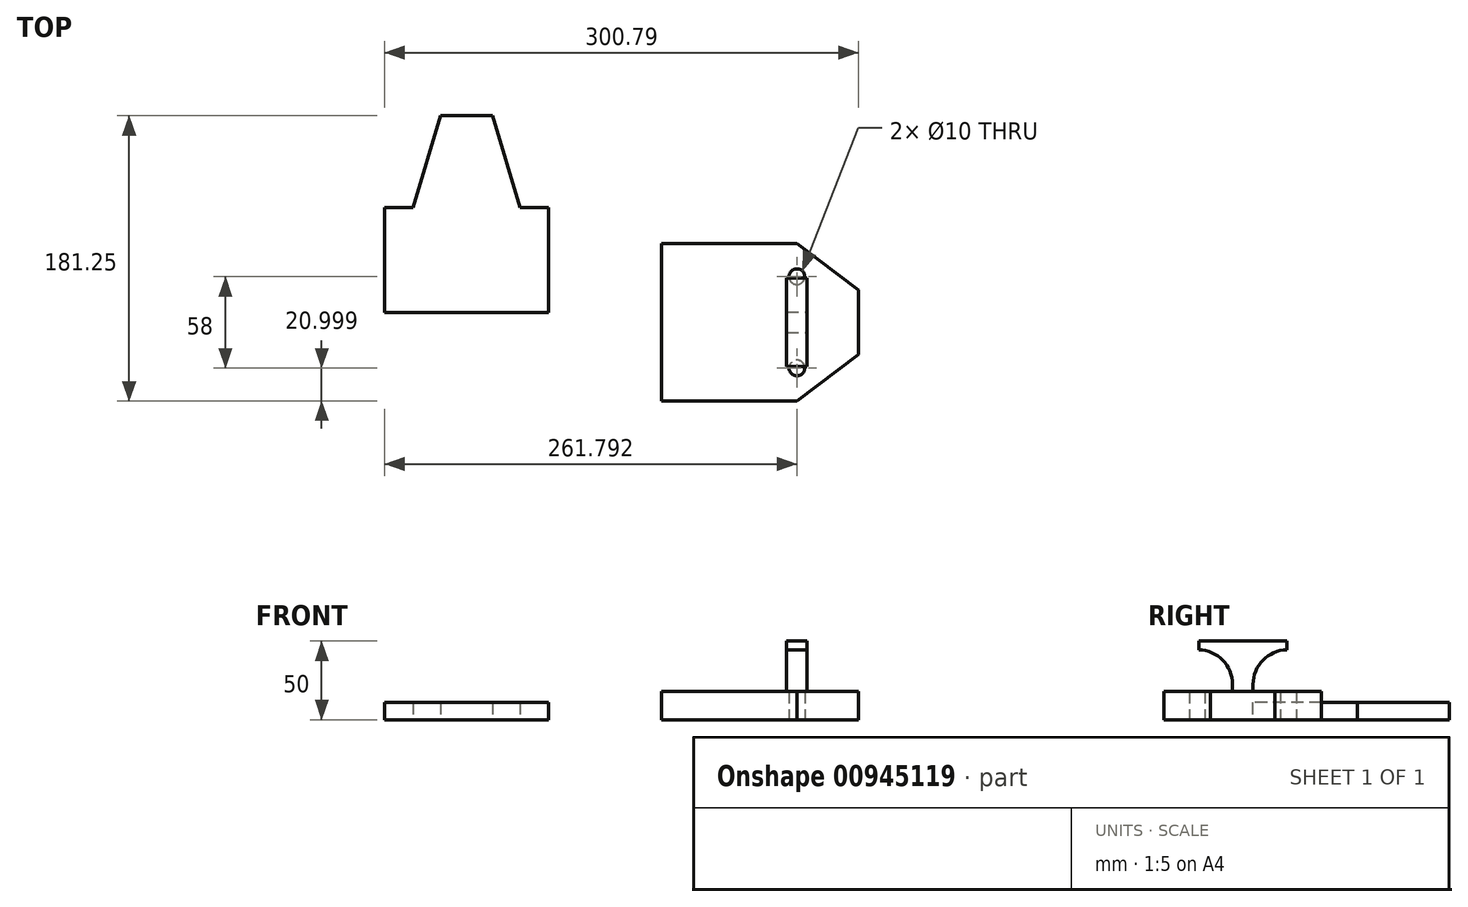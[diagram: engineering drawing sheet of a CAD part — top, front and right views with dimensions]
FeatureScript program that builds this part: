
annotation { "Feature Type Name" : "Feature", "Feature Type Description" : "" }
export const myFeature = defineFeature(function(context is Context, id is Id, definition is map)
    precondition{}
    {
        {
            var Q0;
            Q0=qCreatedBy(makeId("Top.planeOp"),FACE);
            var sketch = newSketch(context, id + "F0", { "sketchPlane" : qUnion([Q0])});
            skLineSegment(sketch, "E0.bottom", {"start": v(-75.9, 31.73) * mm, "end": v(28.1, 31.73) * mm});
            skLineSegment(sketch, "E0.top", {"start": v(-75.9, -34.77) * mm, "end": v(28.1, -34.77) * mm});
            skLineSegment(sketch, "E0.left", {"start": v(-75.9, 31.73) * mm, "end": v(-75.9, -34.77) * mm});
            skLineSegment(sketch, "E0.right", {"start": v(28.1, 31.73) * mm, "end": v(28.1, -34.77) * mm});
            skLineSegment(sketch, "E1", {"start": v(-23.9, -34.77) * mm, "end": v(-23.9, 90.23) * mm});
            skLineSegment(sketch, "E2", {"start": v(-23.9, 90.23) * mm, "end": v(-40.4, 90.23) * mm});
            skLineSegment(sketch, "E3", {"start": v(-23.9, 90.23) * mm, "end": v(-7.4, 90.23) * mm});
            skLineSegment(sketch, "E4", {"start": v(-23.9, 31.73) * mm, "end": v(-57.9, 31.73) * mm});
            skLineSegment(sketch, "E5", {"start": v(-23.9, 31.73) * mm, "end": v(10.1, 31.73) * mm});
            skLineSegment(sketch, "E6", {"start": v(10.1, 31.73) * mm, "end": v(-7.4, 90.23) * mm});
            skLineSegment(sketch, "E7.MirrorCS", {"start": v(-57.9, 31.73) * mm, "end": v(-40.4, 90.23) * mm});
            skSolve(sketch);
        }
        {
            var Q0;
            {var subQ0=sQuery(id+"F0.wireOp",EDGE,"E2");Q0=makeQuery(id+"F0.imprint","IMPRINT",FACE,{"disambiguationData":[TD([[makeQuery(id+"F0.imprint","IMPRINT",EDGE,{"derivedFrom":subQ0}),1.0]])]});}
            var Q1;
            {var subQ0=sQuery(id+"F0.wireOp",EDGE,"E3");Q1=makeQuery(id+"F0.imprint","IMPRINT",FACE,{"disambiguationData":[TD([[makeQuery(id+"F0.imprint","IMPRINT",EDGE,{"derivedFrom":subQ0}),-1.0]])]});}
            var Q2;
            {var subQ0=sQuery(id+"F0.wireOp",EDGE,"E0.right");Q2=makeQuery(id+"F0.imprint","IMPRINT",FACE,{"disambiguationData":[TD([[makeQuery(id+"F0.imprint","IMPRINT",EDGE,{"derivedFrom":subQ0}),-1.0]])]});}
            var Q3;
            {var subQ4=sQuery(id+"F0.wireOp",EDGE,"E0.left");Q3=makeQuery(id+"F0.imprint","IMPRINT",FACE,{"disambiguationData":[TD([[makeQuery(id+"F0.imprint","IMPRINT",EDGE,{"derivedFrom":subQ4}),1.0]])]});}
            extrude(context, id + "F1", {"entities" : qUnion([Q0, Q1, Q2, Q3]), "depth" : 11 * mm, "offsetDistance" : 25 * mm});
        }
        {
            var Q0;
            Q0=qCreatedBy(makeId("Top.planeOp"),FACE);
            var sketch = newSketch(context, id + "F2", { "sketchPlane" : qUnion([Q0])});
            skLineSegment(sketch, "E8.bottom", {"start": v(99.88, 8.98) * mm, "end": v(185.88, 8.98) * mm});
            skLineSegment(sketch, "E8.top", {"start": v(99.88, -91.02) * mm, "end": v(185.88, -91.02) * mm});
            skLineSegment(sketch, "E8.left", {"start": v(99.88, 8.98) * mm, "end": v(99.88, -91.02) * mm});
            skLineSegment(sketch, "E8.right", {"start": v(185.88, 8.98) * mm, "end": v(185.88, -91.02) * mm});
            skLineSegment(sketch, "E9", {"start": v(99.88, -41.02) * mm, "end": v(224.88, -41.02) * mm});
            skLineSegment(sketch, "E10", {"start": v(224.88, -41.02) * mm, "end": v(224.88, -61.52) * mm});
            skLineSegment(sketch, "E11", {"start": v(224.88, -61.52) * mm, "end": v(185.88, -91.02) * mm});
            skLineSegment(sketch, "E12.MirrorCS", {"start": v(224.88, -20.52) * mm, "end": v(185.88, 8.98) * mm});
            skLineSegment(sketch, "E13.MirrorCS", {"start": v(224.88, -41.02) * mm, "end": v(224.88, -20.52) * mm});
            skLineSegment(sketch, "E14.bottom", {"start": v(179.38, -34.52) * mm, "end": v(192.38, -34.52) * mm});
            skLineSegment(sketch, "E14.top", {"start": v(179.38, -47.52) * mm, "end": v(192.38, -47.52) * mm});
            skLineSegment(sketch, "E14.left", {"start": v(179.38, -34.52) * mm, "end": v(179.38, -47.52) * mm});
            skLineSegment(sketch, "E14.right", {"start": v(192.38, -34.52) * mm, "end": v(192.38, -47.52) * mm});
            skPoint(sketch, "E14.middle", {"position": v(185.88, -41.02) * mm});
            skLineSegment(sketch, "E15", {"start": v(185.88, -91.02) * mm, "end": v(185.88, -70.02) * mm});
            skLineSegment(sketch, "E16", {"start": v(185.88, 8.98) * mm, "end": v(185.88, -12.02) * mm});
            skSolve(sketch);
        }
        {
            var Q0;
            {var subQ6=sQuery(id+"F2.wireOp",EDGE,"E8.bottom");Q0=makeQuery(id+"F2.imprint","IMPRINT",FACE,{"disambiguationData":[TD([[makeQuery(id+"F2.imprint","IMPRINT",EDGE,{"derivedFrom":subQ6}),-1.0]])]});}
            var Q1;
            {var subQ1=sQuery(id+"F2.wireOp",EDGE,"E8.top");Q1=makeQuery(id+"F2.imprint","IMPRINT",FACE,{"disambiguationData":[TD([[makeQuery(id+"F2.imprint","IMPRINT",EDGE,{"derivedFrom":subQ1}),1.0]])]});}
            var Q2;
            {var subQ1=sQuery(id+"F2.wireOp",EDGE,"E10");Q2=makeQuery(id+"F2.imprint","IMPRINT",FACE,{"disambiguationData":[TD([[makeQuery(id+"F2.imprint","IMPRINT",EDGE,{"derivedFrom":subQ1}),-1.0]])]});}
            var Q3;
            {var subQ1=sQuery(id+"F2.wireOp",EDGE,"E12.MirrorCS");Q3=makeQuery(id+"F2.imprint","IMPRINT",FACE,{"disambiguationData":[TD([[makeQuery(id+"F2.imprint","IMPRINT",EDGE,{"derivedFrom":subQ1}),1.0]])]});}
            extrude(context, id + "F3", {"entities" : qUnion([Q0, Q1, Q2, Q3]), "depth" : 18 * mm, "offsetDistance" : 25 * mm});
        }
        {
            var Q0;
            {var subQ0=sQuery(id+"F2.wireOp",EDGE,"E14.bottom");var subQ1=sQuery(id+"F2.wireOp",EDGE,"E8.right");var subQ2=makeQuery(id+"F2.imprint","INTERSECT",VERTEX,{"derivedFrom":[subQ1,subQ0]});Q0=makeQuery(id+"F2.imprint","IMPRINT",FACE,{"disambiguationData":[TD([[makeQuery(id+"F2.imprint","IMPRINT",EDGE,{"disambiguationData":[TD([[subQ2,-1.0]])],"derivedFrom":subQ1}),1.0]])]});}
            var Q1;
            {var subQ0=sQuery(id+"F2.wireOp",EDGE,"E14.bottom");var subQ1=sQuery(id+"F2.wireOp",EDGE,"E8.right");var subQ2=makeQuery(id+"F2.imprint","INTERSECT",VERTEX,{"derivedFrom":[subQ1,subQ0]});Q1=makeQuery(id+"F2.imprint","IMPRINT",FACE,{"disambiguationData":[TD([[makeQuery(id+"F2.imprint","IMPRINT",EDGE,{"disambiguationData":[TD([[subQ2,-1.0]])],"derivedFrom":subQ1}),-1.0]])]});}
            var Q2;
            {var subQ0=sQuery(id+"F2.wireOp",EDGE,"E9");var subQ1=sQuery(id+"F2.wireOp",EDGE,"E8.right");var subQ2=makeQuery(id+"F2.imprint","INTERSECT",VERTEX,{"derivedFrom":[subQ1,subQ0]});Q2=makeQuery(id+"F2.imprint","IMPRINT",FACE,{"disambiguationData":[TD([[makeQuery(id+"F2.imprint","IMPRINT",EDGE,{"disambiguationData":[TD([[subQ2,-1.0]])],"derivedFrom":subQ1}),-1.0]])]});}
            var Q3;
            {var subQ0=sQuery(id+"F2.wireOp",EDGE,"E9");var subQ1=sQuery(id+"F2.wireOp",EDGE,"E8.right");var subQ2=makeQuery(id+"F2.imprint","INTERSECT",VERTEX,{"derivedFrom":[subQ1,subQ0]});Q3=makeQuery(id+"F2.imprint","IMPRINT",FACE,{"disambiguationData":[TD([[makeQuery(id+"F2.imprint","IMPRINT",EDGE,{"disambiguationData":[TD([[subQ2,-1.0]])],"derivedFrom":subQ1}),1.0]])]});}
            extrude(context, id + "F4", {"entities" : qUnion([Q0, Q1, Q2, Q3]), "operationType" : NewBodyOperationType.ADD, "depth" : 50 * mm, "offsetDistance" : 25 * mm});
        }
        {
            var Q0;
            Q0=makeQuery(id+"F4.opExtrude","SWEPT_FACE",FACE,{"disambiguationData":[OSD([sQuery(id+"F2.wireOp",EDGE,"E14.right")])]});
            var sketch = newSketch(context, id + "F5", { "sketchPlane" : qUnion([Q0])});
            skLineSegment(sketch, "E17", {"start": v(-47.52, 50) * mm, "end": v(-47.52, 44.5) * mm});
            skLineSegment(sketch, "E18", {"start": v(-47.52, 44.5) * mm, "end": v(-69.02, 44.5) * mm});
            skLineSegment(sketch, "E19", {"start": v(-69.02, 44.5) * mm, "end": v(-69.02, 50) * mm});
            skLineSegment(sketch, "E20", {"start": v(-69.02, 50) * mm, "end": v(-47.52, 50) * mm});
            skLineSegment(sketch, "E21", {"start": v(-41.02, 50) * mm, "end": v(-41.02, 18) * mm});
            skLineSegment(sketch, "E22.MirrorCS", {"start": v(-13.02, 50) * mm, "end": v(-34.52, 50) * mm});
            skLineSegment(sketch, "E23.MirrorCS", {"start": v(-13.02, 44.5) * mm, "end": v(-12.52, 44.5) * mm});
            skLineSegment(sketch, "E24.MirrorCS", {"start": v(-13.02, 44.5) * mm, "end": v(-13.02, 50) * mm});
            skLineSegment(sketch, "E25.bottom", {"start": v(-69.52, 44.5) * mm, "end": v(-69.02, 44.5) * mm});
            skLineSegment(sketch, "E25.top", {"start": v(-69.02, 18) * mm, "end": v(-47.52, 18) * mm});
            skLineSegment(sketch, "E25.left", {"start": v(-69.02, 44.5) * mm, "end": v(-69.02, 18) * mm});
            skLineSegment(sketch, "E25.right", {"start": v(-47.52, 22.5) * mm, "end": v(-47.52, 18) * mm});
            skLineSegment(sketch, "E26.bottom", {"start": v(-13.02, 44.5) * mm, "end": v(-34.52, 44.5) * mm});
            skLineSegment(sketch, "E26.top", {"start": v(-13.02, 18) * mm, "end": v(-34.52, 18) * mm});
            skLineSegment(sketch, "E26.left", {"start": v(-13.02, 44.5) * mm, "end": v(-13.02, 18) * mm});
            skLineSegment(sketch, "E26.right", {"start": v(-34.52, 22.5) * mm, "end": v(-34.52, 18) * mm});
            skPoint(sketch, "E27.visualSharp", {"position": v(-47.52, 44.5) * mm});
            skArc(sketch, "E27.filletArc", {"start": v(-47.52, 22.5) * mm, "mid": v(-53.96, 38.06) * mm, "end": v(-69.52, 44.5) * mm});
            skPoint(sketch, "E28.visualSharp", {"position": v(-34.52, 44.5) * mm});
            skArc(sketch, "E28.filletArc", {"start": v(-12.52, 44.5) * mm, "mid": v(-28.08, 38.06) * mm, "end": v(-34.52, 22.5) * mm});
            skSolve(sketch);
        }
        {
            var Q0;
            Q0=makeQuery(id+"F5.imprint","IMPRINT",FACE,{"disambiguationData":[TD([[makeQuery(id+"F5.imprint","IMPRINT",EDGE,{"derivedFrom":sQuery(id+"F5.wireOp",EDGE,"E17")}),-1.0]])]});
            var Q1;
            {var subQ0=sQuery(id+"F5.wireOp",EDGE,"E22.MirrorCS");Q1=makeQuery(id+"F5.imprint","IMPRINT",FACE,{"disambiguationData":[TD([[makeQuery(id+"F5.imprint","IMPRINT",EDGE,{"derivedFrom":subQ0}),1.0]])]});}
            var Q2;
            {var subQ0=sQuery(id+"F5.wireOp",EDGE,"E18");Q2=makeQuery(id+"F5.imprint","IMPRINT",FACE,{"disambiguationData":[TD([[makeQuery(id+"F5.imprint","IMPRINT",EDGE,{"derivedFrom":subQ0}),1.0]])]});}
            var Q3;
            {var subQ0=sQuery(id+"F5.wireOp",EDGE,"E26.bottom");Q3=makeQuery(id+"F5.imprint","IMPRINT",FACE,{"disambiguationData":[TD([[makeQuery(id+"F5.imprint","IMPRINT",EDGE,{"derivedFrom":subQ0}),1.0]])]});}
            extrude(context, id + "F6", {"entities" : qUnion([Q0, Q1, Q2, Q3]), "operationType" : NewBodyOperationType.ADD, "oppositeDirection" : true, "depth" : 13 * mm, "offsetDistance" : 25 * mm});
        }
        {
            var Q0;
            Q0=sQuery(id+"F2.wireOp",VERTEX,"E15.end");
            var Q1;
            Q1=sQuery(id+"F2.wireOp",VERTEX,"E16.end");
            var Q2;
            Q2=makeQuery(id+"F3.opExtrude","SWEPT_BODY",BODY,{"disambiguationData":[OSD([sQuery(id+"F2.wireOp",EDGE,"E8.bottom"),sQuery(id+"F2.wireOp",EDGE,"E8.top"),sQuery(id+"F2.wireOp",EDGE,"E8.left"),sQuery(id+"F2.wireOp",EDGE,"E10"),sQuery(id+"F2.wireOp",EDGE,"E11"),sQuery(id+"F2.wireOp",EDGE,"E12.MirrorCS"),sQuery(id+"F2.wireOp",EDGE,"E13.MirrorCS"),sQuery(id+"F2.wireOp",EDGE,"E14.bottom"),sQuery(id+"F2.wireOp",EDGE,"E14.top"),sQuery(id+"F2.wireOp",EDGE,"E14.left"),sQuery(id+"F2.wireOp",EDGE,"E14.right")])]});
            hole(context, id + "F7", {"style" : HoleStyle.SIMPLE, "endStyle" : HoleEndStyle.BLIND, "oppositeDirection" : true, "holeDiameter" : 10 * mm, "majorDiameter" : 5 * mm, "holeDepth" : 20 * mm, "isTappedThrough" : true, "tappedDepth" : 12 * mm, "tapClearance" : 3, "locations" : qUnion([Q0, Q1]), "scope" : qUnion([Q2])});
        }
    });
